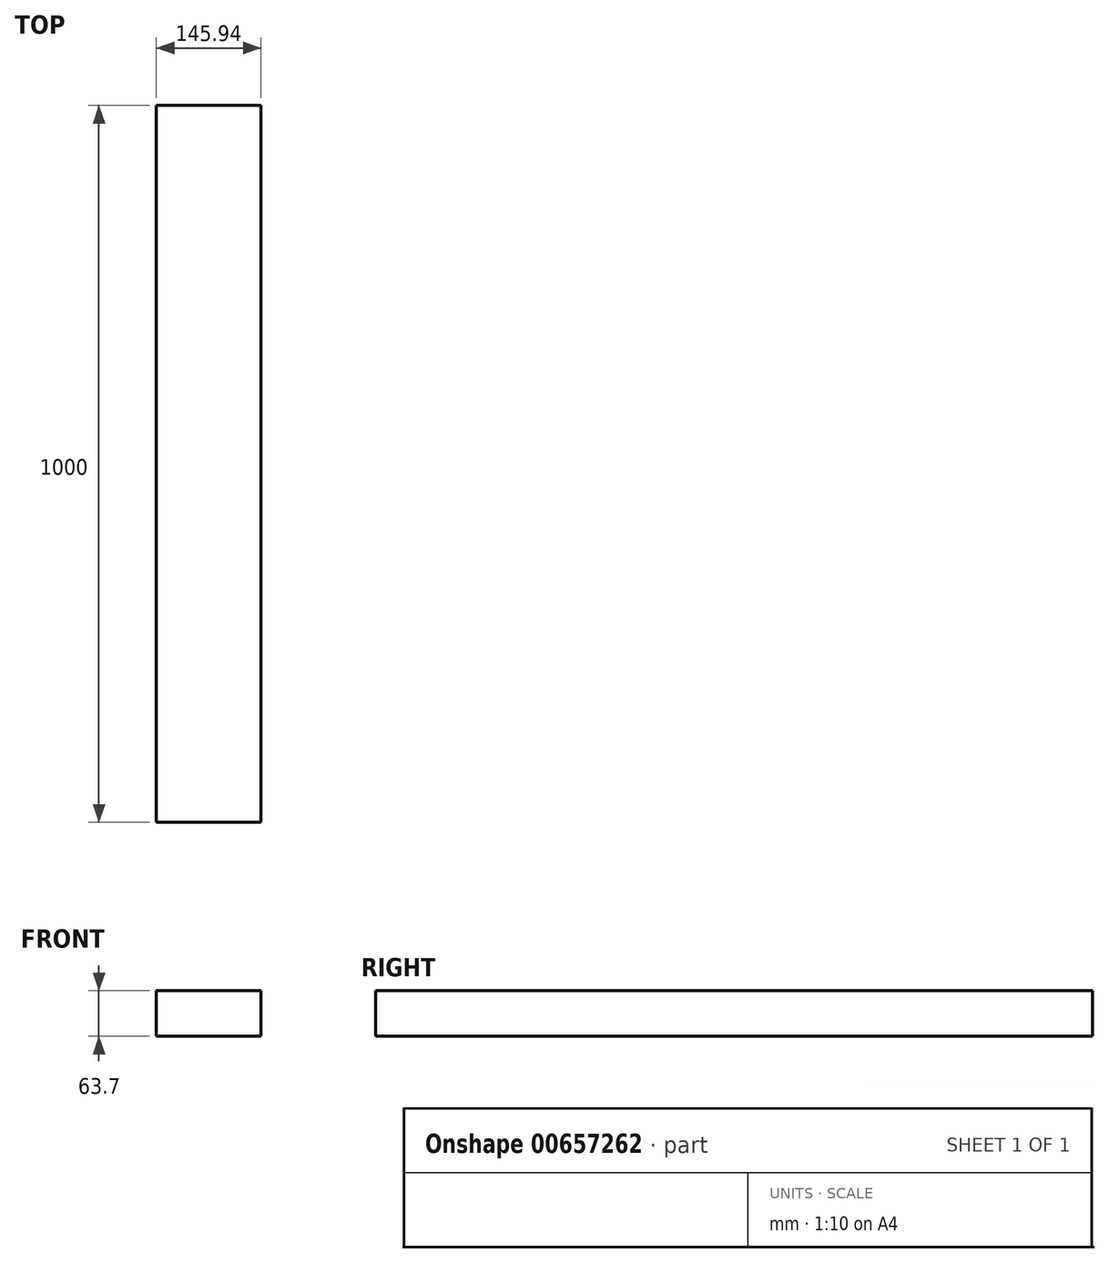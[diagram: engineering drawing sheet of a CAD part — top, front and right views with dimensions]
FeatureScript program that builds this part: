
annotation { "Feature Type Name" : "Feature", "Feature Type Description" : "" }
export const myFeature = defineFeature(function(context is Context, id is Id, definition is map)
    precondition{}
    {
        {
            var Q0;
            Q0=qCreatedBy(makeId("Front.planeOp"),FACE);
            var sketch = newSketch(context, id + "F0", { "sketchPlane" : qUnion([Q0])});
            skLineSegment(sketch, "E0.bottom", {"start": v(72.97, -31.85) * mm, "end": v(-72.97, -31.85) * mm});
            skLineSegment(sketch, "E0.top", {"start": v(72.97, 31.85) * mm, "end": v(-72.97, 31.85) * mm});
            skLineSegment(sketch, "E0.left", {"start": v(72.97, -31.85) * mm, "end": v(72.97, 31.85) * mm});
            skLineSegment(sketch, "E0.right", {"start": v(-72.97, -31.85) * mm, "end": v(-72.97, 31.85) * mm});
            skPoint(sketch, "E0.middle", {"position": v(0, 0) * mm});
            skSolve(sketch);
        }
        {
            var Q0;
            Q0 = qSketchRegion(id + "F0", true);
            extrude(context, id + "F1", {"entities" : qUnion([Q0]), "endBound" : BoundingType.SYMMETRIC, "depth" : 1000 * mm, "offsetDistance" : 25.4 * mm});
        }
    });
